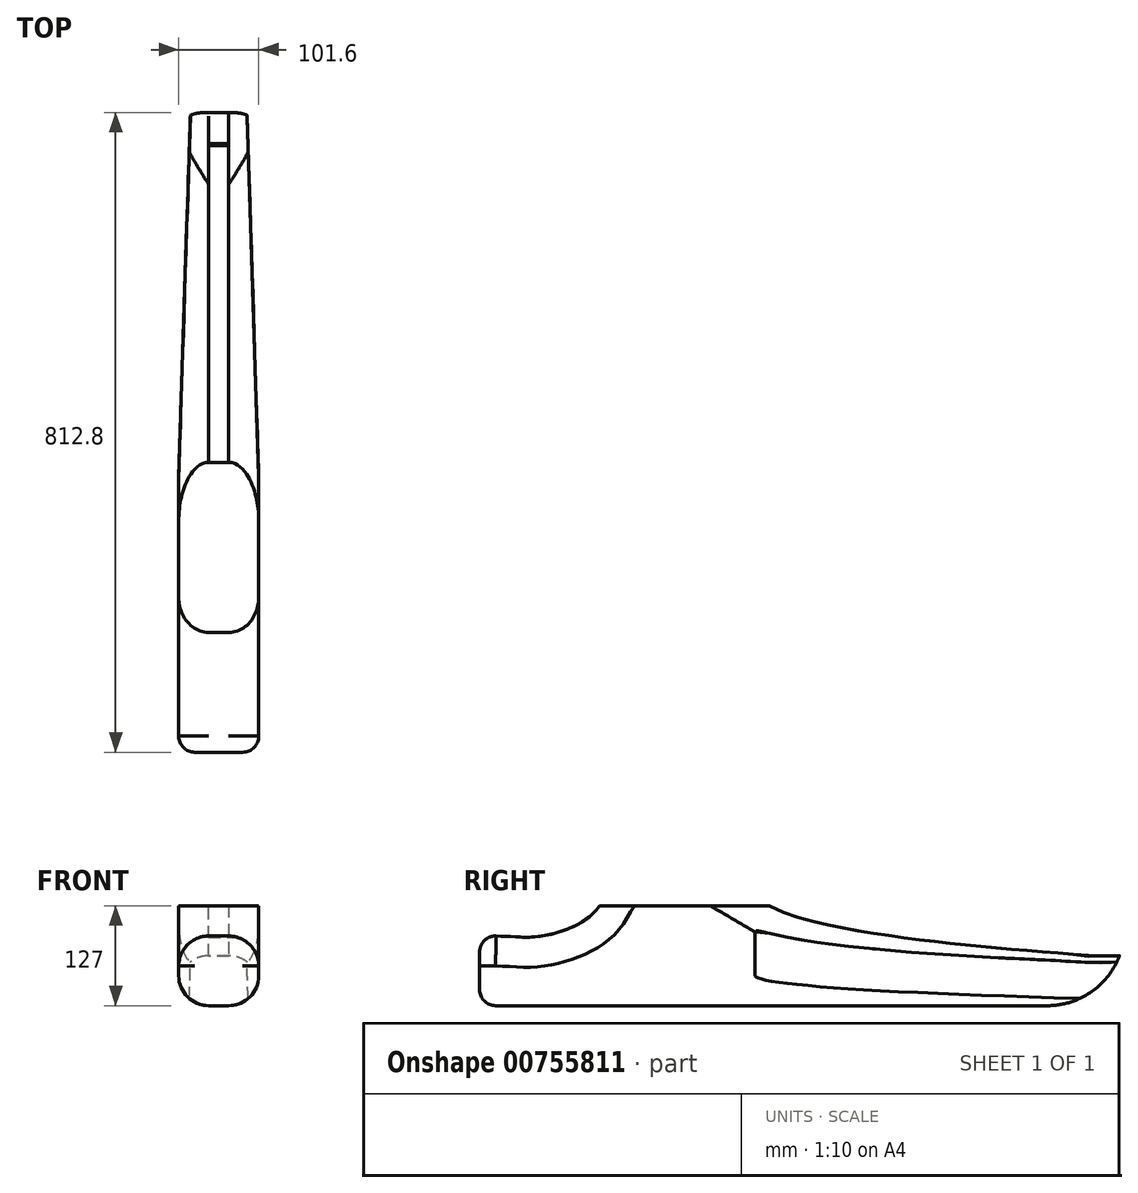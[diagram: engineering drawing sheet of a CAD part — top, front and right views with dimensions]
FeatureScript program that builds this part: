
annotation { "Feature Type Name" : "Feature", "Feature Type Description" : "" }
export const myFeature = defineFeature(function(context is Context, id is Id, definition is map)
    precondition{}
    {
        {
            var Q0;
            Q0=qCreatedBy(makeId("Right.planeOp"),FACE);
            var sketch = newSketch(context, id + "F0", { "sketchPlane" : qUnion([Q0])});
            skLineSegment(sketch, "E0.bottom", {"start": v(0, 119.4) * mm, "end": v(215.9, 119.4) * mm});
            skLineSegment(sketch, "E0.top", {"start": v(-152.2, -7.6) * mm, "end": v(660.6, -7.6) * mm});
            skLineSegment(sketch, "E0.left", {"start": v(-152.2, 81.3) * mm, "end": v(-152.2, -7.6) * mm});
            skLineSegment(sketch, "E0.right", {"start": v(660.6, 55.9) * mm, "end": v(660.6, -7.6) * mm});
            skPoint(sketch, "E1", {"position": v(660.6, 55.9) * mm});
            skPoint(sketch, "E2", {"position": v(-152.2, 81.3) * mm});
            skFitSpline(sketch, "E3", {"points": [v(660.6, 55.9) * mm, v(620.2, 55.9) * mm, v(215.9, 119.4) * mm], "startDerivative": vector(-781.33, -14.03) * mm, "endDerivative": vector(-301.92, 177.6) * mm});
            skFitSpline(sketch, "E4", {"points": [v(-152.2, 81.3) * mm, v(-70.4, 81.3) * mm, v(0, 119.4) * mm], "startDerivative": vector(258.58, 0) * mm, "endDerivative": vector(75.06, 126.98) * mm});
            skSolve(sketch);
        }
        {
            var Q0;
            Q0=qSketchRegion(id+"F0",true);
            extrude(context, id + "F1", {"entities" : qUnion([Q0]), "depth" : 101.6 * mm, "offsetDistance" : 25.4 * mm});
        }
        {
            var Q0;
            Q0=makeQuery(id+"F1.opExtrude","CAP_EDGE",EDGE,{"disambiguationData":[OSD([sQuery(id+"F0.wireOp",EDGE,"E4")])],"isStart":false});
            var Q1;
            Q1=makeQuery(id+"F1.opExtrude","CAP_EDGE",EDGE,{"disambiguationData":[OSD([sQuery(id+"F0.wireOp",EDGE,"E4")])],"isStart":true});
            fillet(context, id + "F2", {"entities" : qUnion([Q0, Q1]), "radius" : 38.1 * mm, "tangentPropagation" : true, "allowEdgeOverflow" : false});
        }
        {
            var Q0;
            Q0=makeQuery(id+"F1.opExtrude","CAP_EDGE",EDGE,{"disambiguationData":[OSD([sQuery(id+"F0.wireOp",EDGE,"E0.top")])],"isStart":false});
            var Q1;
            Q1=makeQuery(id+"F1.opExtrude","CAP_EDGE",EDGE,{"disambiguationData":[OSD([sQuery(id+"F0.wireOp",EDGE,"E0.top")])],"isStart":true});
            fillet(context, id + "F3", {"entities" : qUnion([Q0, Q1]), "radius" : 38.1 * mm, "tangentPropagation" : true, "allowEdgeOverflow" : false});
        }
        {
            var Q0;
            Q0=makeQuery(id+"F1.opExtrude","CAP_EDGE",EDGE,{"disambiguationData":[OSD([sQuery(id+"F0.wireOp",EDGE,"E3")])],"isStart":false});
            var Q1;
            Q1=makeQuery(id+"F1.opExtrude","CAP_EDGE",EDGE,{"disambiguationData":[OSD([sQuery(id+"F0.wireOp",EDGE,"E3")])],"isStart":true});
            fillet(context, id + "F4", {"entities" : qUnion([Q0, Q1]), "radius" : 38.1 * mm, "tangentPropagation" : true, "allowEdgeOverflow" : false});
        }
        {
            var Q0;
            Q0=makeQuery(id+"F2.opFillet","BLEND_EDGE",EDGE,{"blendedFrom":[makeQuery(id+"F1.opExtrude","CAP_EDGE",EDGE,{"disambiguationData":[OSD([sQuery(id+"F0.wireOp",EDGE,"E4")])],"isStart":false}),makeQuery(id+"F1.opExtrude","SWEPT_FACE",FACE,{"disambiguationData":[OSD([sQuery(id+"F0.wireOp",EDGE,"E0.left")])]})],"blendedInto":[makeQuery(id+"F1.opExtrude","SWEPT_FACE",FACE,{"disambiguationData":[OSD([sQuery(id+"F0.wireOp",EDGE,"E0.left")])]})]});
            var Q1;
            Q1=makeQuery(id+"F2.opFillet","BLEND_EDGE",EDGE,{"blendedFrom":[makeQuery(id+"F1.opExtrude","CAP_EDGE",EDGE,{"disambiguationData":[OSD([sQuery(id+"F0.wireOp",EDGE,"E4")])],"isStart":true}),makeQuery(id+"F1.opExtrude","SWEPT_FACE",FACE,{"disambiguationData":[OSD([sQuery(id+"F0.wireOp",EDGE,"E0.left")])]})],"blendedInto":[makeQuery(id+"F1.opExtrude","SWEPT_FACE",FACE,{"disambiguationData":[OSD([sQuery(id+"F0.wireOp",EDGE,"E0.left")])]})]});
            var Q2;
            Q2=makeQuery(id+"F1.opExtrude","SWEPT_EDGE",EDGE,{"disambiguationData":[OSD([sQuery(id+"F0.wireOp",EDGE,"E0.left"),sQuery(id+"F0.wireOp",EDGE,"E4")])]});
            var Q3;
            Q3=makeQuery(id+"F3.opFillet","BLEND_EDGE",EDGE,{"blendedFrom":[makeQuery(id+"F1.opExtrude","CAP_EDGE",EDGE,{"disambiguationData":[OSD([sQuery(id+"F0.wireOp",EDGE,"E0.top")])],"isStart":false}),makeQuery(id+"F1.opExtrude","SWEPT_FACE",FACE,{"disambiguationData":[OSD([sQuery(id+"F0.wireOp",EDGE,"E0.left")])]})],"blendedInto":[makeQuery(id+"F1.opExtrude","SWEPT_FACE",FACE,{"disambiguationData":[OSD([sQuery(id+"F0.wireOp",EDGE,"E0.left")])]})]});
            var Q4;
            Q4=makeQuery(id+"F1.opExtrude","CAP_EDGE",EDGE,{"disambiguationData":[OSD([sQuery(id+"F0.wireOp",EDGE,"E0.left")])],"isStart":false});
            var Q5;
            Q5=makeQuery(id+"F3.opFillet","BLEND_EDGE",EDGE,{"blendedFrom":[makeQuery(id+"F1.opExtrude","CAP_EDGE",EDGE,{"disambiguationData":[OSD([sQuery(id+"F0.wireOp",EDGE,"E0.top")])],"isStart":true}),makeQuery(id+"F1.opExtrude","SWEPT_FACE",FACE,{"disambiguationData":[OSD([sQuery(id+"F0.wireOp",EDGE,"E0.left")])]})],"blendedInto":[makeQuery(id+"F1.opExtrude","SWEPT_FACE",FACE,{"disambiguationData":[OSD([sQuery(id+"F0.wireOp",EDGE,"E0.left")])]})]});
            var Q6;
            Q6=makeQuery(id+"F1.opExtrude","CAP_EDGE",EDGE,{"disambiguationData":[OSD([sQuery(id+"F0.wireOp",EDGE,"E0.left")])],"isStart":true});
            fillet(context, id + "F5", {"entities" : qUnion([Q0, Q1, Q2, Q3, Q4, Q5, Q6]), "radius" : 20.24 * mm, "tangentPropagation" : true, "allowEdgeOverflow" : false});
        }
        {
            var Q0;
            Q0=makeQuery(id+"F3.opFillet","BLEND_EDGE",EDGE,{"blendedFrom":[makeQuery(id+"F1.opExtrude","CAP_EDGE",EDGE,{"disambiguationData":[OSD([sQuery(id+"F0.wireOp",EDGE,"E0.top")])],"isStart":true}),makeQuery(id+"F1.opExtrude","SWEPT_FACE",FACE,{"disambiguationData":[OSD([sQuery(id+"F0.wireOp",EDGE,"E0.right")])]})],"blendedInto":[makeQuery(id+"F1.opExtrude","SWEPT_FACE",FACE,{"disambiguationData":[OSD([sQuery(id+"F0.wireOp",EDGE,"E0.right")])]})]});
            var Q1;
            Q1=makeQuery(id+"F1.opExtrude","SWEPT_EDGE",EDGE,{"disambiguationData":[OSD([sQuery(id+"F0.wireOp",EDGE,"E0.top"),sQuery(id+"F0.wireOp",EDGE,"E0.right")])]});
            var Q2;
            Q2=makeQuery(id+"F3.opFillet","BLEND_EDGE",EDGE,{"blendedFrom":[makeQuery(id+"F1.opExtrude","CAP_EDGE",EDGE,{"disambiguationData":[OSD([sQuery(id+"F0.wireOp",EDGE,"E0.top")])],"isStart":false}),makeQuery(id+"F1.opExtrude","SWEPT_FACE",FACE,{"disambiguationData":[OSD([sQuery(id+"F0.wireOp",EDGE,"E0.right")])]})],"blendedInto":[makeQuery(id+"F1.opExtrude","SWEPT_FACE",FACE,{"disambiguationData":[OSD([sQuery(id+"F0.wireOp",EDGE,"E0.right")])]})]});
            fillet(context, id + "F6", {"entities" : qUnion([Q0, Q1, Q2]), "radius" : 98.11 * mm, "tangentPropagation" : true, "allowEdgeOverflow" : false});
        }
        {
            var Q0;
            Q0=makeQuery(id+"F1.opExtrude","SWEPT_FACE",FACE,{"disambiguationData":[OSD([sQuery(id+"F0.wireOp",EDGE,"E0.top")])]});
            var sketch = newSketch(context, id + "F7", { "sketchPlane" : qUnion([Q0])});
            skLineSegment(sketch, "E5", {"start": v(-17.2, -667.46) * mm, "end": v(15.14, -667.46) * mm});
            skLineSegment(sketch, "E6", {"start": v(15.14, -667.46) * mm, "end": v(0, -197.77) * mm});
            skLineSegment(sketch, "E7", {"start": v(0, -197.77) * mm, "end": v(-17.2, -667.46) * mm});
            skLineSegment(sketch, "E8.MirrorCS", {"start": v(118.8, -667.46) * mm, "end": v(86.46, -667.46) * mm});
            skLineSegment(sketch, "E9.MirrorCS", {"start": v(86.46, -667.46) * mm, "end": v(101.6, -197.77) * mm});
            skLineSegment(sketch, "E10.MirrorCS", {"start": v(101.6, -197.77) * mm, "end": v(118.8, -667.46) * mm});
            skPoint(sketch, "E11.start.orphan", {"position": v(50.8, 131.96) * mm});
            skSolve(sketch);
        }
        {
            var Q0;
            Q0 = qSketchRegion(id + "F7", true);
            extrude(context, id + "F8", {"entities" : qUnion([Q0]), "operationType" : NewBodyOperationType.REMOVE, "endBound" : BoundingType.THROUGH_ALL, "oppositeDirection" : true, "depth" : 25.4 * mm, "offsetDistance" : 25.4 * mm});
        }
    });
